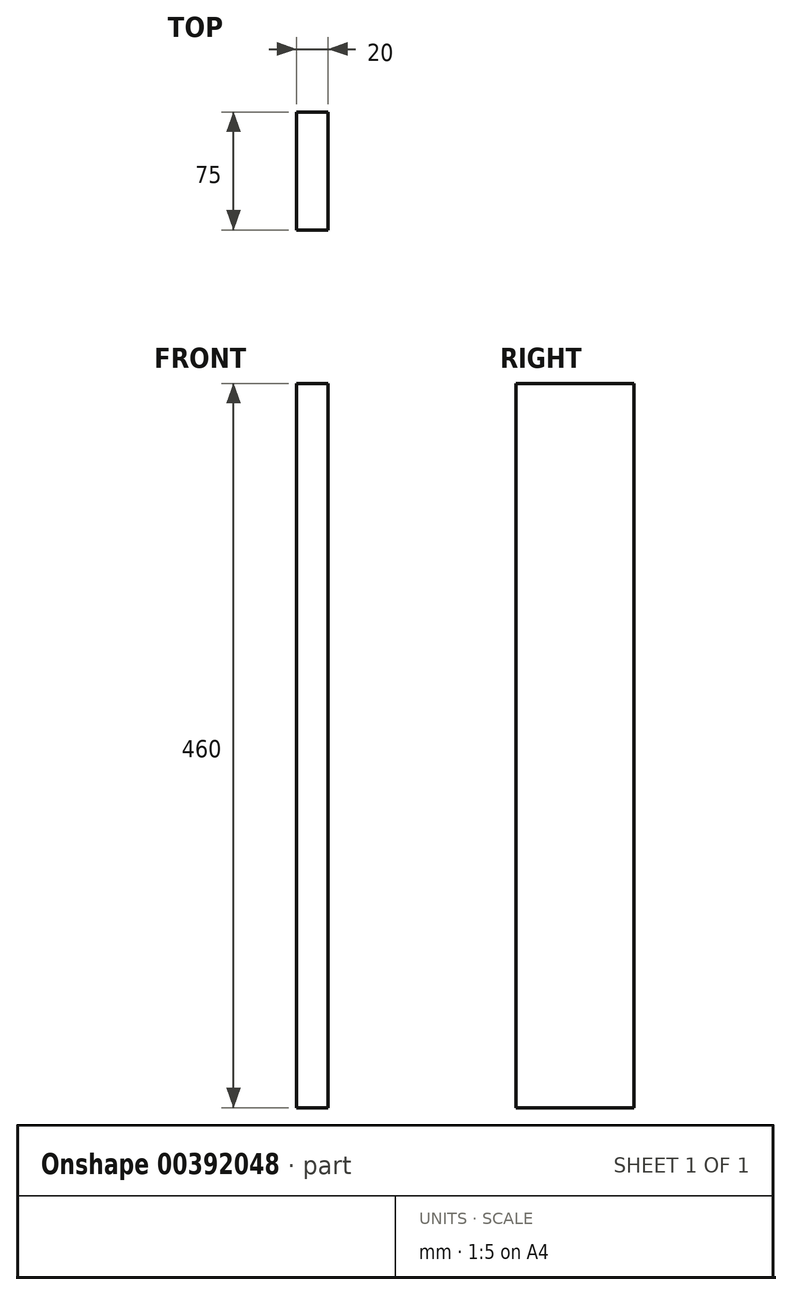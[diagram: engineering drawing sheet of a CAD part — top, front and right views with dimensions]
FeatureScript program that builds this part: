
annotation { "Feature Type Name" : "Feature", "Feature Type Description" : "" }
export const myFeature = defineFeature(function(context is Context, id is Id, definition is map)
    precondition{}
    {
        {
            var Q0;
            Q0=qCreatedBy(makeId("Top.planeOp"),FACE);
            var sketch = newSketch(context, id + "F0", { "sketchPlane" : qUnion([Q0])});
            skLineSegment(sketch, "E0.bottom", {"start": v(-10, 37.5) * mm, "end": v(10, 37.5) * mm});
            skLineSegment(sketch, "E0.top", {"start": v(-10, -37.5) * mm, "end": v(10, -37.5) * mm});
            skLineSegment(sketch, "E0.left", {"start": v(-10, 37.5) * mm, "end": v(-10, -37.5) * mm});
            skLineSegment(sketch, "E0.right", {"start": v(10, 37.5) * mm, "end": v(10, -37.5) * mm});
            skPoint(sketch, "E0.middle", {"position": v(0, 0) * mm});
            skSolve(sketch);
        }
        {
            var Q0;
            Q0=makeQuery(id+"F0.imprint","IMPRINT",FACE,{"disambiguationData":[TD([[makeQuery(id+"F0.imprint","IMPRINT",EDGE,{"derivedFrom":sQuery(id+"F0.wireOp",EDGE,"E0.bottom")}),-1.0]])]});
            extrude(context, id + "F1", {"entities" : qUnion([Q0]), "endBound" : BoundingType.SYMMETRIC, "depth" : 460 * mm});
        }
    });
